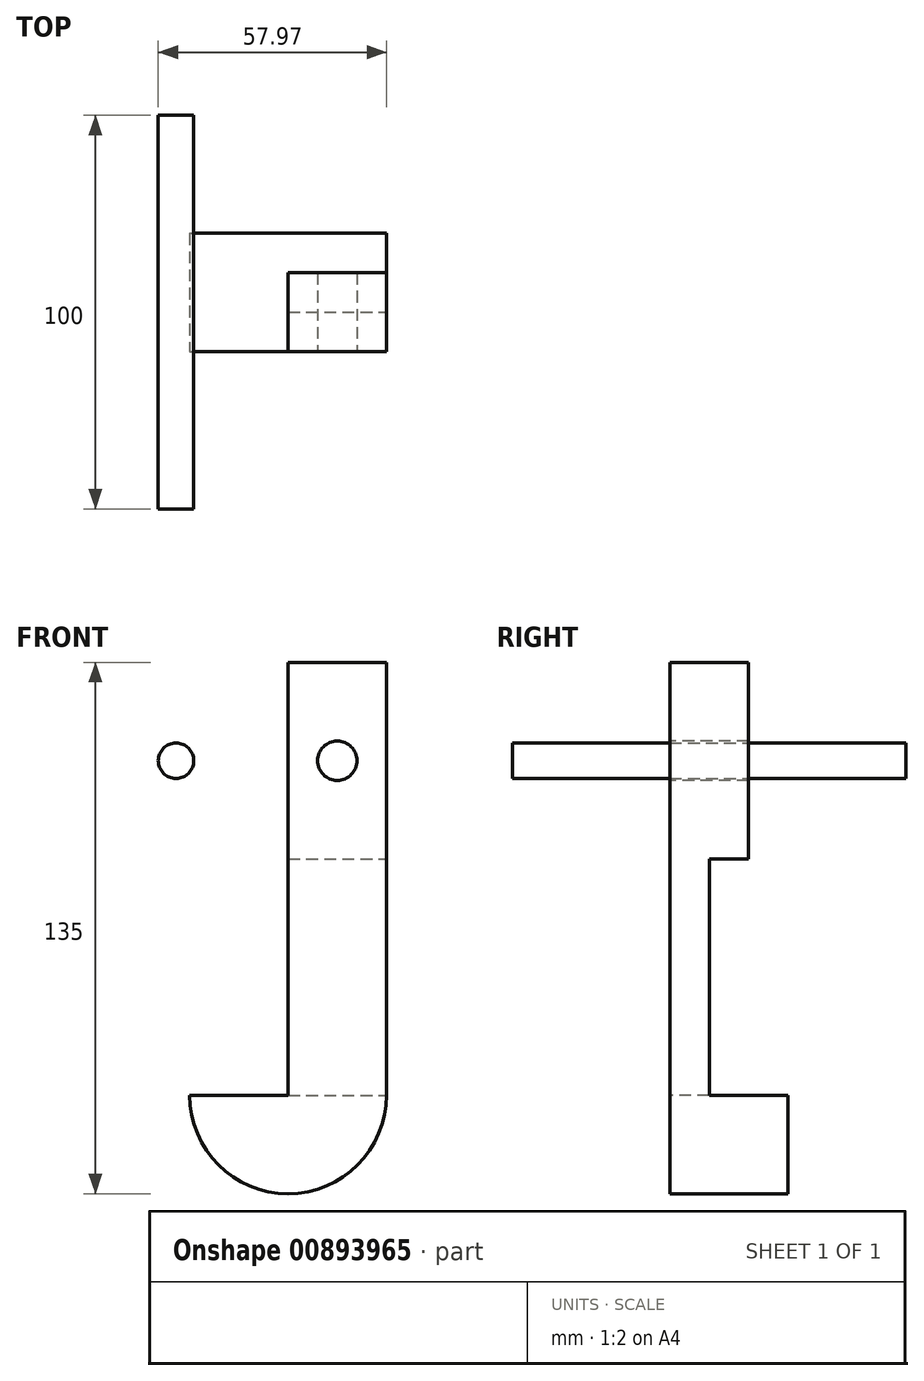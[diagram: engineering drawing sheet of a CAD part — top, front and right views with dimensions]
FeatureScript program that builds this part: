
annotation { "Feature Type Name" : "Feature", "Feature Type Description" : "" }
export const myFeature = defineFeature(function(context is Context, id is Id, definition is map)
    precondition{}
    {
        {
            var Q0;
            Q0=qCreatedBy(makeId("Front.planeOp"),FACE);
            var sketch = newSketch(context, id + "F0", { "sketchPlane" : qUnion([Q0])});
            skCircle(sketch, "E0", {"center": v(-23.54, 0) * mm, "radius": 4.5 * mm});
            skSolve(sketch);
        }
        {
            var Q0;
            Q0 = qSketchRegion(id + "F0", true);
            extrude(context, id + "F1", {"entities" : qUnion([Q0]), "endBound" : BoundingType.SYMMETRIC, "depth" : 100 * mm, "offsetDistance" : 25 * mm});
        }
        {
            var Q0;
            Q0=qCreatedBy(makeId("Front.planeOp"),FACE);
            var sketch = newSketch(context, id + "F2", { "sketchPlane" : qUnion([Q0])});
            skLineSegment(sketch, "E1.bottom", {"start": v(4.93, 25) * mm, "end": v(29.93, 25) * mm});
            skLineSegment(sketch, "E1.top", {"start": v(4.93, -25) * mm, "end": v(29.93, -25) * mm});
            skLineSegment(sketch, "E1.left", {"start": v(4.93, 25) * mm, "end": v(4.93, -25) * mm});
            skLineSegment(sketch, "E1.right", {"start": v(29.93, 25) * mm, "end": v(29.93, -25) * mm});
            skPoint(sketch, "E1.middle", {"position": v(17.43, 0) * mm});
            skSolve(sketch);
        }
        {
            var Q0;
            Q0 = qSketchRegion(id + "F2", true);
            extrude(context, id + "F3", {"entities" : qUnion([Q0]), "endBound" : BoundingType.SYMMETRIC, "depth" : 20 * mm, "offsetDistance" : 25 * mm});
        }
        {
            var Q0;
            Q0=makeQuery(id+"F3.opExtrude","CAP_FACE",FACE,{"disambiguationData":[OSD([sQuery(id+"F2.wireOp",EDGE,"E1.bottom"),sQuery(id+"F2.wireOp",EDGE,"E1.top"),sQuery(id+"F2.wireOp",EDGE,"E1.left"),sQuery(id+"F2.wireOp",EDGE,"E1.right")])],"isStart":false});
            var sketch = newSketch(context, id + "F4", { "sketchPlane" : qUnion([Q0])});
            skLineSegment(sketch, "E2.bottom", {"start": v(4.93, -25) * mm, "end": v(29.93, -25) * mm});
            skLineSegment(sketch, "E2.top", {"start": v(4.93, -85) * mm, "end": v(29.93, -85) * mm});
            skLineSegment(sketch, "E2.left", {"start": v(4.93, -25) * mm, "end": v(4.93, -85) * mm});
            skLineSegment(sketch, "E2.right", {"start": v(29.93, -25) * mm, "end": v(29.93, -85) * mm});
            skSolve(sketch);
        }
        {
            var Q0;
            Q0 = qSketchRegion(id + "F4", true);
            extrude(context, id + "F5", {"entities" : qUnion([Q0]), "operationType" : NewBodyOperationType.ADD, "oppositeDirection" : true, "depth" : 10 * mm, "offsetDistance" : 25 * mm});
        }
        {
            var Q0;
            Q0=makeQuery(id+"F5.boolean.opBoolean","MERGE",FACE,{"derivedFrom":[makeQuery(id+"F3.opExtrude","CAP_FACE",FACE,{"disambiguationData":[OSD([sQuery(id+"F2.wireOp",EDGE,"E1.bottom"),sQuery(id+"F2.wireOp",EDGE,"E1.top"),sQuery(id+"F2.wireOp",EDGE,"E1.left"),sQuery(id+"F2.wireOp",EDGE,"E1.right")])],"isStart":false}),makeQuery(id+"F5.opExtrude","CAP_FACE",FACE,{"disambiguationData":[OSD([sQuery(id+"F4.wireOp",EDGE,"E2.bottom"),sQuery(id+"F4.wireOp",EDGE,"E2.top"),sQuery(id+"F4.wireOp",EDGE,"E2.left"),sQuery(id+"F4.wireOp",EDGE,"E2.right")])],"isStart":true})]});
            var sketch = newSketch(context, id + "F6", { "sketchPlane" : qUnion([Q0])});
            skArc(sketch, "E3", {"start": v(29.93, -85) * mm, "mid": v(4.93, -110) * mm, "end": v(-20.07, -85) * mm});
            skLineSegment(sketch, "E4", {"start": v(-20.07, -85) * mm, "end": v(4.93, -85) * mm});
            skLineSegment(sketch, "E5", {"start": v(4.93, -85) * mm, "end": v(29.93, -85) * mm});
            skSolve(sketch);
        }
        {
            var Q0;
            Q0 = qSketchRegion(id + "F6", true);
            extrude(context, id + "F7", {"entities" : qUnion([Q0]), "operationType" : NewBodyOperationType.ADD, "oppositeDirection" : true, "depth" : 30 * mm, "offsetDistance" : 25 * mm});
        }
        {
            var Q0;
            Q0=makeQuery(id+"F7.boolean.opBoolean","MERGE",FACE,{"derivedFrom":[makeQuery(id+"F5.boolean.opBoolean","MERGE",FACE,{"derivedFrom":[makeQuery(id+"F3.opExtrude","CAP_FACE",FACE,{"disambiguationData":[OSD([sQuery(id+"F2.wireOp",EDGE,"E1.bottom"),sQuery(id+"F2.wireOp",EDGE,"E1.top"),sQuery(id+"F2.wireOp",EDGE,"E1.left"),sQuery(id+"F2.wireOp",EDGE,"E1.right")])],"isStart":false}),makeQuery(id+"F5.opExtrude","CAP_FACE",FACE,{"disambiguationData":[OSD([sQuery(id+"F4.wireOp",EDGE,"E2.bottom"),sQuery(id+"F4.wireOp",EDGE,"E2.top"),sQuery(id+"F4.wireOp",EDGE,"E2.left"),sQuery(id+"F4.wireOp",EDGE,"E2.right")])],"isStart":true})]}),makeQuery(id+"F7.opExtrude","CAP_FACE",FACE,{"disambiguationData":[OSD([sQuery(id+"F6.wireOp",EDGE,"E3"),sQuery(id+"F6.wireOp",EDGE,"E4"),sQuery(id+"F6.wireOp",EDGE,"E5")])],"isStart":true})]});
            var sketch = newSketch(context, id + "F8", { "sketchPlane" : qUnion([Q0])});
            skCircle(sketch, "E6", {"center": v(17.43, 0) * mm, "radius": 5 * mm});
            skSolve(sketch);
        }
        {
            var Q0;
            Q0 = qSketchRegion(id + "F8", true);
            extrude(context, id + "F9", {"entities" : qUnion([Q0]), "operationType" : NewBodyOperationType.REMOVE, "endBound" : BoundingType.THROUGH_ALL, "oppositeDirection" : true, "depth" : 25 * mm, "offsetDistance" : 25 * mm});
        }
    });
